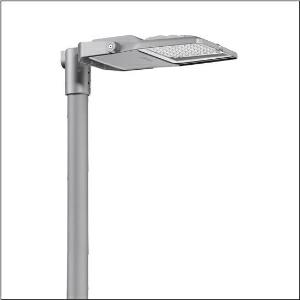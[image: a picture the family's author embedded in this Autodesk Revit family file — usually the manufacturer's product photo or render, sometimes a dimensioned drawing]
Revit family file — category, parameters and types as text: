
# Revit family: floodlight_fl_21_iq_mini___pl64_5xa7771d2e3a_d262
name_source: partatom
category: Lighting Fixtures
units: mm (PartAtom-declared; Revit-internal decimal feet)

## family parameters
Cut with Voids When Loaded = No
Host = Face
Light Source = No
Part Type = Normal
Room Calculation Point = No
Round Connector Dimension = Use Diameter
Shared = No

## types (1)
- --- (1 x LED, 17220 lm, 143 W, 3000K)
    Apparent Load = 143 VA
    CIE Flux Codes = 28 80 98 100 100
    Color Rendering = 70
    Color Temperature = 3000K
    Default Elevation = 1800 mm
    Description = Floodlight FL 21 iQ mini, floodlight, primary light control with lens, of PMMA, primary optical cover: protective disc, of toughened safety glass, transparent, light distribution: PL64, light emission: direct distribution, installation type: surface-mounted, LED, High Power LED, rated luminous flux: 17.220lm, luminous efficacy: 120lm/W, light colour: 730, colour temperature: 3000K, control: Auto-Match, Temp-Guard, Lumen-Switch, Night-Set, Smart-Wire, Light-Fading, Desk-Remote (wireless, voltage-free reading and setting of iQ features in the workshop via application-optimized NFC function/RFID function), optimised constant luminous flux control (CLO 2.0), with terminal, 6-pole, mains connection: 220..240V, AC, 50/60Hz, start of lifetime: 143W, end of service life: 152W, reduction: 61W, luminaire housing, of diecast aluminium, powder-coated, Siteco® metallic grey (DB 702S), corrosivity category C5 mid according to DIN EN ISO 12944, sealing non-destructively replaceable, please order mast flange separately, mast bracket, of steel, galvanised, powder-coated, Siteco® metallic grey (DB 702S), protection rating (complete): IP66, insulation class (complete): insulation class II (safety insulation), certification: CE, ENEC, VDE, protection symbol: D, impact resistance: IK08, permissible operating ambient temperature: -40..+40°C, permissible operating ambient temperature for outdoor applications: -40..+50°C, standard: DIN EN 12944, LABS conformity tested according to VDMA 24364:2018-05, packaging unit: 1 piece

Light Distribution: PL64
    Height = 70 mm
    Lamp = 1 x LED
    Lamp Light Flux = 17220 lm
    Lamp Power = 143 W
    Lamp count = 1
    Length = 485 mm
    Luminous efficacy = 120 lm/W
    Manufacturer = Siteco
    ModVariant = No
    Model = 5XA7771D2E3A
    Number of Poles = 1
    OnlyDefault = Yes
    Power Factor = 1
    Product Name = Floodlight FL 21 iQ mini | PL64
    Product group = floodlight | pylon annexe
    ProductGroupID = 6200
    Protection Class = Protection class II
    Protection Degree = IP 66
    RLX_Detail_Level = 1
    RLX_Emergency_Light_Flux = 0 lm
    RLX_Emergency_Type = 0
    RLX_Emergency_Type_DB = No
    RlxData = <blob elided: 101505 chars, md5=b0657b34>
    Socket = socket
    Standby Power = 0 W
    System Light Flux = 17220 lm
    System Power = 143 W
    Type Comments = factory setting: luminous flux: 100 % | dim-lin: 254 | 730 mA
    Type Image = l_1007125.jpg
    URL = http://relux.com
    VarID = @adj_098367
    Voltage = 0 V
    Weight = 0.00 kg
    Width = 337 mm

## geometry (parser evidence)
native form markers: Blend x4, Sweep x12
no freeform markers — native parametric forms only
